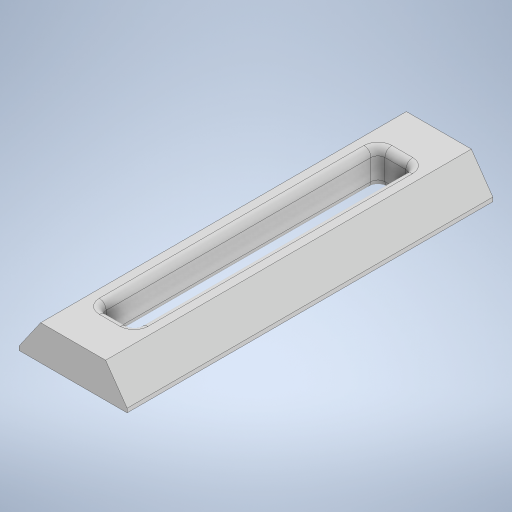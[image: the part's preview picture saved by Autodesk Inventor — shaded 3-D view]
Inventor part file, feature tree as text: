
AUTODESK INVENTOR PART (.ipt)
format: ipt  version: 2023 (Build 270158000, 158)  size: 283,648 bytes
history: native  units: mm
features: extrude x2, fillet x2, sketch x2
ambient origin geometry x8: Origin, YZ Plane, XZ Plane, XY Plane, X Axis, Y Axis, Z Axis, Center Point
bodies: Solido1 (feature_tree)
feature tree (6):
  extrude  "Estrusione1"  Depth=31.0mm
  extrude  "Estrusione2"  Depth=10.0mm
  fillet  "Raccordo1"  Radius=21.0mm
  fillet  "Raccordo2"  Radius=4.0mm
  sketch  "Schizzo1"
  sketch  "Schizzo3"
